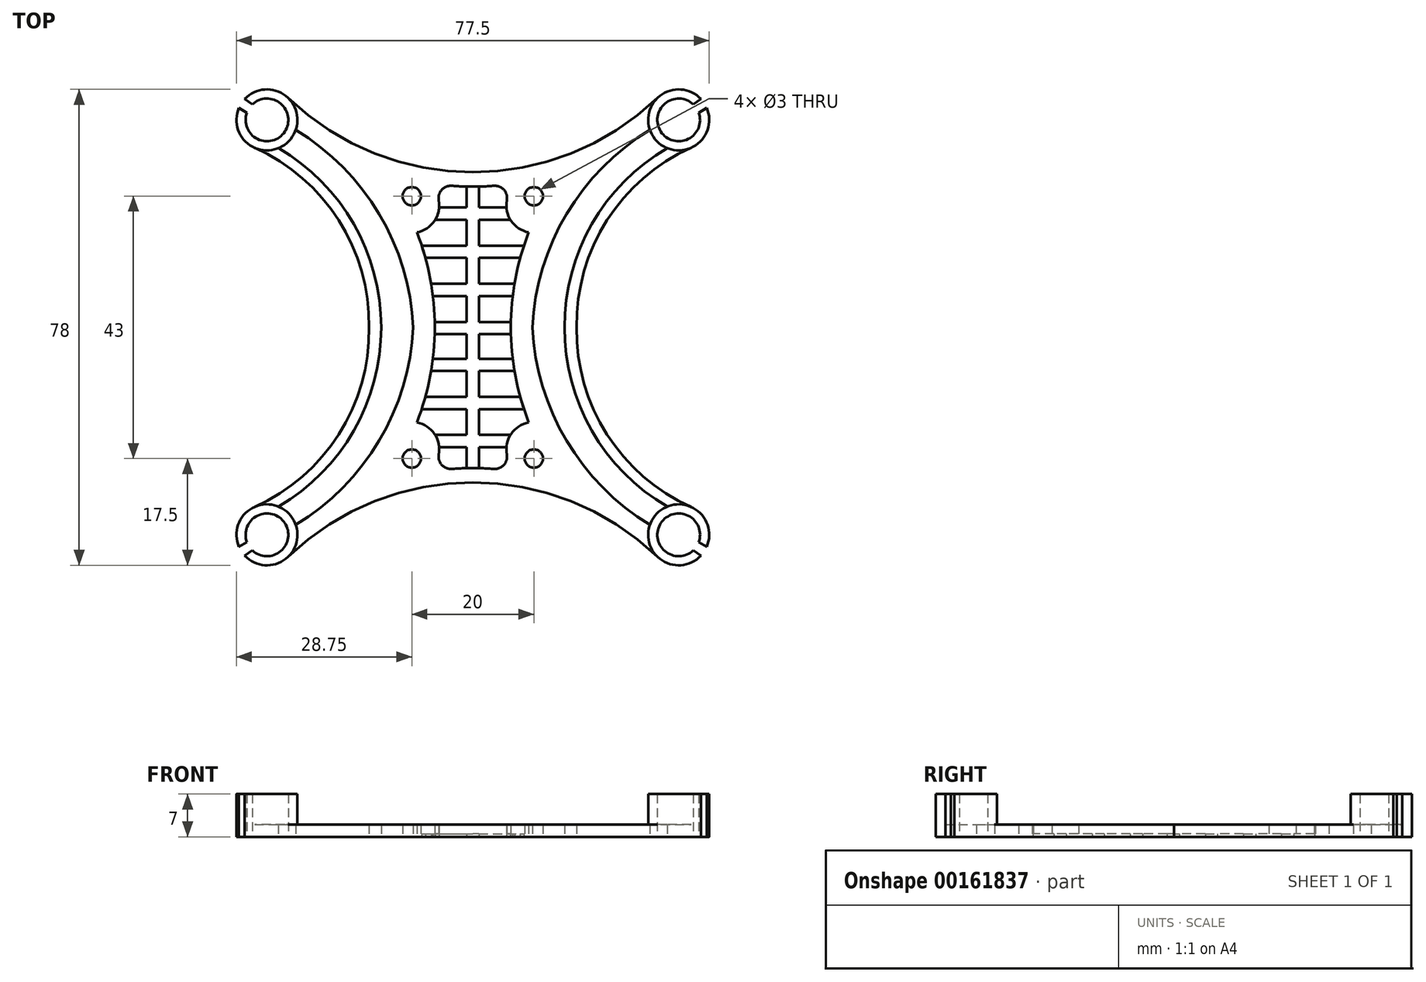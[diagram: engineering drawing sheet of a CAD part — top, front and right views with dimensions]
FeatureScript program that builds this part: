
annotation { "Feature Type Name" : "Feature", "Feature Type Description" : "" }
export const myFeature = defineFeature(function(context is Context, id is Id, definition is map)
    precondition{}
    {
        {
            var Q0;
            Q0=qCreatedBy(makeId("Top.planeOp"),FACE);
            var sketch = newSketch(context, id + "F0", { "sketchPlane" : qUnion([Q0])});
            skArc(sketch, "E0", {"start": v(37.04, -35.18) * mm, "mid": v(30.82, -32.08) * mm, "end": v(36.14, -36.56) * mm});
            skCircle(sketch, "E1", {"center": v(10, -21.5) * mm, "radius": 1.5 * mm});
            skArc(sketch, "E2", {"start": v(17.02, 0.03) * mm, "mid": v(21.97, -17.52) * mm, "end": v(35.78, -29.44) * mm});
            skLineSegment(sketch, "E3.MirrorCS", {"start": v(37.04, -35.18) * mm, "end": v(38.34, -35.99) * mm});
            skLineSegment(sketch, "E4.MirrorCS", {"start": v(36.14, -36.56) * mm, "end": v(37.39, -37.43) * mm});
            skArc(sketch, "E5.0", {"start": v(9.76, 0) * mm, "mid": v(15.37, -18.58) * mm, "end": v(29.04, -32.36) * mm});
            skArc(sketch, "E6.trimOffspring", {"start": v(9.16, -15.58) * mm, "mid": v(6.28, -17.47) * mm, "end": v(5.58, -20.84) * mm});
            skArc(sketch, "E7.trimOffspring", {"start": v(6.23, 0) * mm, "mid": v(6.97, -7.93) * mm, "end": v(9.16, -15.58) * mm});
            skArc(sketch, "E8.trimOffspring", {"start": v(0, -23.07) * mm, "mid": v(1.73, -23.1) * mm, "end": v(3.46, -23.2) * mm});
            skPoint(sketch, "E9.visualSharp", {"position": v(7.4, -23.67) * mm});
            skArc(sketch, "E9.filletArc", {"start": v(3.46, -23.2) * mm, "mid": v(5.1, -22.54) * mm, "end": v(5.58, -20.84) * mm});
            skArc(sketch, "E10.trimOffspring", {"start": v(15.01, 0) * mm, "mid": v(19.52, -16.95) * mm, "end": v(31.88, -29.4) * mm});
            skArc(sketch, "E11.trimOffspring", {"start": v(31.88, -29.4) * mm, "mid": v(30.14, -30.57) * mm, "end": v(29.04, -32.36) * mm});
            skArc(sketch, "E12.trimOffspring", {"start": v(38.34, -35.99) * mm, "mid": v(38.4, -32.19) * mm, "end": v(35.78, -29.44) * mm});
            skArc(sketch, "E13.MirrorCS", {"start": v(38.34, -35.99) * mm, "mid": v(38.74, -33.77) * mm, "end": v(38.13, -31.6) * mm});
            skArc(sketch, "E14.trimOffspring", {"start": v(30.28, -37.6) * mm, "mid": v(33.87, -39) * mm, "end": v(37.39, -37.43) * mm});
            skArc(sketch, "E15.MirrorCS", {"start": v(0, -23.07) * mm, "mid": v(-1.73, -23.1) * mm, "end": v(-3.46, -23.2) * mm});
            skLineSegment(sketch, "E16.MirrorCS", {"start": v(-36.14, -36.56) * mm, "end": v(-37.39, -37.43) * mm});
            skArc(sketch, "E17.MirrorCS", {"start": v(-34.5, -38.95) * mm, "mid": v(-36.07, -38.43) * mm, "end": v(-37.39, -37.43) * mm});
            skLineSegment(sketch, "E18.MirrorCS", {"start": v(-37.04, -35.18) * mm, "end": v(-38.34, -35.99) * mm});
            skArc(sketch, "E19.MirrorCS", {"start": v(-38.34, -35.99) * mm, "mid": v(-38.4, -32.19) * mm, "end": v(-35.78, -29.44) * mm});
            skArc(sketch, "E20.MirrorCS", {"start": v(-3.46, -23.2) * mm, "mid": v(-5.1, -22.54) * mm, "end": v(-5.58, -20.84) * mm});
            skArc(sketch, "E21.MirrorCS", {"start": v(-31.88, -29.4) * mm, "mid": v(-30.14, -30.57) * mm, "end": v(-29.04, -32.36) * mm});
            skArc(sketch, "E22.MirrorCS", {"start": v(-30.28, -37.6) * mm, "mid": v(-33.87, -39) * mm, "end": v(-37.39, -37.43) * mm});
            skArc(sketch, "E23.MirrorCS", {"start": v(-37.22, -30.41) * mm, "mid": v(-36.55, -29.86) * mm, "end": v(-35.78, -29.44) * mm});
            skCircle(sketch, "E24.MirrorC", {"center": v(-10, -21.5) * mm, "radius": 1.5 * mm});
            skArc(sketch, "E25.MirrorCS", {"start": v(-6.23, 0) * mm, "mid": v(-6.97, -7.93) * mm, "end": v(-9.16, -15.58) * mm});
            skArc(sketch, "E26.MirrorCS", {"start": v(-9.16, -15.58) * mm, "mid": v(-6.28, -17.47) * mm, "end": v(-5.58, -20.84) * mm});
            skPoint(sketch, "E27.MirrorP", {"position": v(-7.4, -23.67) * mm});
            skArc(sketch, "E28.MirrorCS", {"start": v(-9.76, 0) * mm, "mid": v(-15.37, -18.58) * mm, "end": v(-29.04, -32.36) * mm});
            skArc(sketch, "E29.MirrorCS", {"start": v(-37.04, -35.18) * mm, "mid": v(-30.82, -32.08) * mm, "end": v(-36.14, -36.56) * mm});
            skArc(sketch, "E30.MirrorCS", {"start": v(-17.02, 0.03) * mm, "mid": v(-21.97, -17.52) * mm, "end": v(-35.78, -29.44) * mm});
            skArc(sketch, "E31.MirrorCS", {"start": v(-15.01, 0) * mm, "mid": v(-19.52, -16.95) * mm, "end": v(-31.88, -29.4) * mm});
            skArc(sketch, "E32.MirrorCS", {"start": v(0, 23.07) * mm, "mid": v(1.73, 23.1) * mm, "end": v(3.46, 23.2) * mm});
            skArc(sketch, "E33.MirrorCS", {"start": v(0, 23.07) * mm, "mid": v(-1.73, 23.1) * mm, "end": v(-3.46, 23.2) * mm});
            skLineSegment(sketch, "E34.MirrorCS", {"start": v(-37.04, 35.18) * mm, "end": v(-38.34, 35.99) * mm});
            skLineSegment(sketch, "E35.MirrorCS", {"start": v(37.04, 35.18) * mm, "end": v(38.34, 35.99) * mm});
            skArc(sketch, "E36.MirrorCS", {"start": v(3.46, 23.2) * mm, "mid": v(5.1, 22.54) * mm, "end": v(5.58, 20.84) * mm});
            skLineSegment(sketch, "E37.MirrorCS", {"start": v(-36.14, 36.56) * mm, "end": v(-37.39, 37.43) * mm});
            skArc(sketch, "E38.MirrorCS", {"start": v(-30.28, 37.6) * mm, "mid": v(-33.87, 39) * mm, "end": v(-37.39, 37.43) * mm});
            skArc(sketch, "E39.MirrorCS", {"start": v(34.5, 38.95) * mm, "mid": v(36.07, 38.43) * mm, "end": v(37.39, 37.43) * mm});
            skLineSegment(sketch, "E40.MirrorCS", {"start": v(36.14, 36.56) * mm, "end": v(37.39, 37.43) * mm});
            skArc(sketch, "E41.MirrorCS", {"start": v(30.28, 37.6) * mm, "mid": v(33.87, 39) * mm, "end": v(37.39, 37.43) * mm});
            skArc(sketch, "E42.MirrorCS", {"start": v(-31.88, 29.4) * mm, "mid": v(-30.14, 30.57) * mm, "end": v(-29.04, 32.36) * mm});
            skArc(sketch, "E43.MirrorCS", {"start": v(31.88, 29.4) * mm, "mid": v(30.14, 30.57) * mm, "end": v(29.04, 32.36) * mm});
            skArc(sketch, "E44.MirrorCS", {"start": v(-34.5, 38.95) * mm, "mid": v(-36.07, 38.43) * mm, "end": v(-37.39, 37.43) * mm});
            skArc(sketch, "E45.MirrorCS", {"start": v(-3.46, 23.2) * mm, "mid": v(-5.1, 22.54) * mm, "end": v(-5.58, 20.84) * mm});
            skArc(sketch, "E46.MirrorCS", {"start": v(-37.04, 35.18) * mm, "mid": v(-30.82, 32.08) * mm, "end": v(-36.14, 36.56) * mm});
            skArc(sketch, "E47.MirrorCS", {"start": v(-38.34, 35.99) * mm, "mid": v(-38.4, 32.19) * mm, "end": v(-35.78, 29.44) * mm});
            skArc(sketch, "E48.MirrorCS", {"start": v(38.34, 35.99) * mm, "mid": v(38.74, 33.77) * mm, "end": v(38.13, 31.6) * mm});
            skArc(sketch, "E49.MirrorCS", {"start": v(37.04, 35.18) * mm, "mid": v(30.82, 32.08) * mm, "end": v(36.14, 36.56) * mm});
            skArc(sketch, "E50.MirrorCS", {"start": v(38.34, 35.99) * mm, "mid": v(38.4, 32.19) * mm, "end": v(35.78, 29.44) * mm});
            skCircle(sketch, "E51.MirrorC", {"center": v(10, 21.5) * mm, "radius": 1.5 * mm});
            skCircle(sketch, "E52.MirrorC", {"center": v(-10, 21.5) * mm, "radius": 1.5 * mm});
            skArc(sketch, "E53.MirrorCS", {"start": v(-38.34, 35.99) * mm, "mid": v(-38.74, 33.77) * mm, "end": v(-38.13, 31.6) * mm});
            skPoint(sketch, "E54.MirrorP", {"position": v(-7.4, 23.67) * mm});
            skPoint(sketch, "E55.MirrorP", {"position": v(7.4, 23.67) * mm});
            skArc(sketch, "E56.MirrorCS", {"start": v(-15.01, 0) * mm, "mid": v(-19.52, 16.95) * mm, "end": v(-31.88, 29.4) * mm});
            skArc(sketch, "E57.MirrorCS", {"start": v(6.23, 0) * mm, "mid": v(6.97, 7.93) * mm, "end": v(9.16, 15.58) * mm});
            skArc(sketch, "E58.MirrorCS", {"start": v(-6.23, 0) * mm, "mid": v(-6.97, 7.93) * mm, "end": v(-9.16, 15.58) * mm});
            skArc(sketch, "E59.MirrorCS", {"start": v(-17.02, -0.03) * mm, "mid": v(-21.97, 17.52) * mm, "end": v(-35.78, 29.44) * mm});
            skArc(sketch, "E60.MirrorCS", {"start": v(-9.76, 0) * mm, "mid": v(-15.37, 18.58) * mm, "end": v(-29.04, 32.36) * mm});
            skArc(sketch, "E61.MirrorCS", {"start": v(15.01, 0) * mm, "mid": v(19.52, 16.95) * mm, "end": v(31.88, 29.4) * mm});
            skArc(sketch, "E62.MirrorCS", {"start": v(9.76, 0) * mm, "mid": v(15.37, 18.58) * mm, "end": v(29.04, 32.36) * mm});
            skArc(sketch, "E63.MirrorCS", {"start": v(9.16, 15.58) * mm, "mid": v(6.28, 17.47) * mm, "end": v(5.58, 20.84) * mm});
            skArc(sketch, "E64.MirrorCS", {"start": v(-9.16, 15.58) * mm, "mid": v(-6.28, 17.47) * mm, "end": v(-5.58, 20.84) * mm});
            skArc(sketch, "E65.MirrorCS", {"start": v(17.02, -0.03) * mm, "mid": v(21.97, 17.52) * mm, "end": v(35.78, 29.44) * mm});
            skArc(sketch, "E66", {"start": v(-30.28, 37.6) * mm, "mid": v(0, 25.42) * mm, "end": v(30.28, 37.6) * mm});
            skPoint(sketch, "E67.MirrorCS.start.orphan", {"position": v(0, 25.42) * mm});
            skArc(sketch, "E68.MirrorCS", {"start": v(-30.28, -37.6) * mm, "mid": v(0, -25.42) * mm, "end": v(30.28, -37.6) * mm});
            skSolve(sketch);
        }
        {
            var Q0;
            Q0=qSketchRegion(id+"F0",true);
            extrude(context, id + "F1", {"entities" : qUnion([Q0]), "depth" : 2 * mm});
        }
        {
            var Q0;
            Q0=makeQuery(id+"F1.opExtrude","CAP_FACE",FACE,{"disambiguationData":[OSD([sQuery(id+"F0.wireOp",EDGE,"07ed9256-dc37-4db6-ad36-5c41a7523dda2.MirrorCS"),sQuery(id+"F0.wireOp",EDGE,"07ed9256-dc37-4db6-ad36-5c41a7523dda3.MirrorCS"),sQuery(id+"F0.wireOp",EDGE,"07ed9256-dc37-4db6-ad36-5c41a7523dda4.MirrorCS"),sQuery(id+"F0.wireOp",EDGE,"07ed9256-dc37-4db6-ad36-5c41a7523dda5.MirrorCS"),sQuery(id+"F0.wireOp",EDGE,"E9.filletArc"),sQuery(id+"F0.wireOp",EDGE,"E8.trimOffspring"),sQuery(id+"F0.wireOp",EDGE,"07ed9256-dc37-4db6-ad36-5c41a7523dda8.MirrorCS"),sQuery(id+"F0.wireOp",EDGE,"E11.trimOffspring"),sQuery(id+"F0.wireOp",EDGE,"E13.MirrorCS"),sQuery(id+"F0.wireOp",EDGE,"07ed9256-dc37-4db6-ad36-5c41a7523dda11.MirrorCS"),sQuery(id+"F0.wireOp",EDGE,"E4.MirrorCS"),sQuery(id+"F0.wireOp",EDGE,"E3.MirrorCS"),sQuery(id+"F0.wireOp",EDGE,"07ed9256-dc37-4db6-ad36-5c41a7523dda14.MirrorCS"),sQuery(id+"F0.wireOp",EDGE,"E1"),sQuery(id+"F0.wireOp",EDGE,"07ed9256-dc37-4db6-ad36-5c41a7523dda16.MirrorC"),sQuery(id+"F0.wireOp",EDGE,"07ed9256-dc37-4db6-ad36-5c41a7523dda17.MirrorCS"),sQuery(id+"F0.wireOp",EDGE,"07ed9256-dc37-4db6-ad36-5c41a7523dda18.MirrorCS"),sQuery(id+"F0.wireOp",EDGE,"07ed9256-dc37-4db6-ad36-5c41a7523dda19.MirrorCS"),sQuery(id+"F0.wireOp",EDGE,"E10.trimOffspring"),sQuery(id+"F0.wireOp",EDGE,"07ed9256-dc37-4db6-ad36-5c41a7523dda21.MirrorCS"),sQuery(id+"F0.wireOp",EDGE,"07ed9256-dc37-4db6-ad36-5c41a7523dda22.MirrorCS"),sQuery(id+"F0.wireOp",EDGE,"07ed9256-dc37-4db6-ad36-5c41a7523dda23.MirrorCS"),sQuery(id+"F0.wireOp",EDGE,"E5.0"),sQuery(id+"F0.wireOp",EDGE,"E0"),sQuery(id+"F0.wireOp",EDGE,"E6.trimOffspring"),sQuery(id+"F0.wireOp",EDGE,"E2"),sQuery(id+"F0.wireOp",EDGE,"07ed9256-dc37-4db6-ad36-5c41a7523dda29.MirrorCS"),sQuery(id+"F0.wireOp",EDGE,"E7.trimOffspring"),sQuery(id+"F0.wireOp",EDGE,"07ed9256-dc37-4db6-ad36-5c41a7523dda31.MirrorCS"),sQuery(id+"F0.wireOp",EDGE,"07ed9256-dc37-4db6-ad36-5c41a7523dda33.MirrorCS"),sQuery(id+"F0.wireOp",EDGE,"966d41c8-d036-42bd-8d6f-7643b6f02c428.MirrorCS"),sQuery(id+"F0.wireOp",EDGE,"966d41c8-d036-42bd-8d6f-7643b6f02c429.MirrorCS"),sQuery(id+"F0.wireOp",EDGE,"966d41c8-d036-42bd-8d6f-7643b6f02c4210.MirrorCS"),sQuery(id+"F0.wireOp",EDGE,"966d41c8-d036-42bd-8d6f-7643b6f02c4211.MirrorCS"),sQuery(id+"F0.wireOp",EDGE,"966d41c8-d036-42bd-8d6f-7643b6f02c4217.MirrorCS"),sQuery(id+"F0.wireOp",EDGE,"966d41c8-d036-42bd-8d6f-7643b6f02c4222.MirrorCS"),sQuery(id+"F0.wireOp",EDGE,"966d41c8-d036-42bd-8d6f-7643b6f02c4225.MirrorCS"),sQuery(id+"F0.wireOp",EDGE,"966d41c8-d036-42bd-8d6f-7643b6f02c4226.MirrorCS"),sQuery(id+"F0.wireOp",EDGE,"966d41c8-d036-42bd-8d6f-7643b6f02c4227.MirrorCS"),sQuery(id+"F0.wireOp",EDGE,"966d41c8-d036-42bd-8d6f-7643b6f02c4228.MirrorCS"),sQuery(id+"F0.wireOp",EDGE,"966d41c8-d036-42bd-8d6f-7643b6f02c4229.MirrorCS"),sQuery(id+"F0.wireOp",EDGE,"966d41c8-d036-42bd-8d6f-7643b6f02c4230.MirrorCS"),sQuery(id+"F0.wireOp",EDGE,"966d41c8-d036-42bd-8d6f-7643b6f02c4231.MirrorCS"),sQuery(id+"F0.wireOp",EDGE,"966d41c8-d036-42bd-8d6f-7643b6f02c4232.MirrorCS"),sQuery(id+"F0.wireOp",EDGE,"966d41c8-d036-42bd-8d6f-7643b6f02c4233.MirrorCS"),sQuery(id+"F0.wireOp",EDGE,"966d41c8-d036-42bd-8d6f-7643b6f02c4236.MirrorC"),sQuery(id+"F0.wireOp",EDGE,"966d41c8-d036-42bd-8d6f-7643b6f02c4237.MirrorC"),sQuery(id+"F0.wireOp",EDGE,"966d41c8-d036-42bd-8d6f-7643b6f02c4253.MirrorCS"),sQuery(id+"F0.wireOp",EDGE,"966d41c8-d036-42bd-8d6f-7643b6f02c4254.MirrorCS"),sQuery(id+"F0.wireOp",EDGE,"966d41c8-d036-42bd-8d6f-7643b6f02c4255.MirrorCS"),sQuery(id+"F0.wireOp",EDGE,"966d41c8-d036-42bd-8d6f-7643b6f02c4256.MirrorCS"),sQuery(id+"F0.wireOp",EDGE,"966d41c8-d036-42bd-8d6f-7643b6f02c4257.MirrorCS"),sQuery(id+"F0.wireOp",EDGE,"966d41c8-d036-42bd-8d6f-7643b6f02c4259.MirrorCS"),sQuery(id+"F0.wireOp",EDGE,"966d41c8-d036-42bd-8d6f-7643b6f02c4260.MirrorCS"),sQuery(id+"F0.wireOp",EDGE,"966d41c8-d036-42bd-8d6f-7643b6f02c4262.MirrorCS"),sQuery(id+"F0.wireOp",EDGE,"966d41c8-d036-42bd-8d6f-7643b6f02c4263.MirrorCS"),sQuery(id+"F0.wireOp",EDGE,"966d41c8-d036-42bd-8d6f-7643b6f02c4264.MirrorCS"),sQuery(id+"F0.wireOp",EDGE,"966d41c8-d036-42bd-8d6f-7643b6f02c4265.MirrorCS"),sQuery(id+"F0.wireOp",EDGE,"966d41c8-d036-42bd-8d6f-7643b6f02c4266.MirrorCS"),sQuery(id+"F0.wireOp",EDGE,"966d41c8-d036-42bd-8d6f-7643b6f02c4267.MirrorCS")])],"isStart":false});
            var sketch = newSketch(context, id + "F2", { "sketchPlane" : qUnion([Q0])});
            skArc(sketch, "E69.0", {"start": v(37.04, -35.18) * mm, "mid": v(30.82, -32.08) * mm, "end": v(36.14, -36.56) * mm});
            skLineSegment(sketch, "E70.0", {"start": v(37.04, -35.18) * mm, "end": v(38.34, -35.99) * mm});
            skLineSegment(sketch, "E70.1", {"start": v(36.14, -36.56) * mm, "end": v(36.14, -36.56) * mm});
            skLineSegment(sketch, "E71.MirrorCS", {"start": v(-37.04, -35.18) * mm, "end": v(-38.34, -35.99) * mm});
            skLineSegment(sketch, "E72.MirrorCS", {"start": v(-36.14, -36.56) * mm, "end": v(-36.14, -36.56) * mm});
            skArc(sketch, "E73.MirrorCS", {"start": v(-37.04, -35.18) * mm, "mid": v(-30.82, -32.08) * mm, "end": v(-36.14, -36.56) * mm});
            skLineSegment(sketch, "E74.MirrorCS", {"start": v(37.04, 35.18) * mm, "end": v(38.34, 35.99) * mm});
            skLineSegment(sketch, "E75.MirrorCS", {"start": v(36.14, 36.56) * mm, "end": v(36.14, 36.56) * mm});
            skLineSegment(sketch, "E76.MirrorCS", {"start": v(-37.04, 35.18) * mm, "end": v(-38.34, 35.99) * mm});
            skLineSegment(sketch, "E77.MirrorCS", {"start": v(-36.14, 36.56) * mm, "end": v(-36.14, 36.56) * mm});
            skArc(sketch, "E78.MirrorCS", {"start": v(-37.04, 35.18) * mm, "mid": v(-30.82, 32.08) * mm, "end": v(-36.14, 36.56) * mm});
            skArc(sketch, "E79.MirrorCS", {"start": v(37.04, 35.18) * mm, "mid": v(30.82, 32.08) * mm, "end": v(36.14, 36.56) * mm});
            skArc(sketch, "E80", {"start": v(38.34, -35.99) * mm, "mid": v(29.57, -31.26) * mm, "end": v(37.39, -37.43) * mm});
            skArc(sketch, "E81", {"start": v(-38.34, 35.99) * mm, "mid": v(-29.57, 31.26) * mm, "end": v(-37.39, 37.43) * mm});
            skArc(sketch, "E82", {"start": v(37.39, 37.43) * mm, "mid": v(29.57, 31.26) * mm, "end": v(38.34, 35.99) * mm});
            skArc(sketch, "E83", {"start": v(-37.39, -37.43) * mm, "mid": v(-29.57, -31.26) * mm, "end": v(-38.34, -35.99) * mm});
            skLineSegment(sketch, "E84", {"start": v(36.14, -36.56) * mm, "end": v(37.39, -37.43) * mm});
            skLineSegment(sketch, "E85", {"start": v(-37.39, -37.43) * mm, "end": v(-36.14, -36.56) * mm});
            skLineSegment(sketch, "E86", {"start": v(36.14, 36.56) * mm, "end": v(37.39, 37.43) * mm});
            skLineSegment(sketch, "E87", {"start": v(-36.14, 36.56) * mm, "end": v(-37.39, 37.43) * mm});
            skSolve(sketch);
        }
        {
            var Q0;
            Q0=qSketchRegion(id+"F2",true);
            extrude(context, id + "F3", {"entities" : qUnion([Q0]), "operationType" : NewBodyOperationType.ADD, "depth" : 5 * mm});
        }
        {
            var Q0;
            Q0=qCreatedBy(makeId("Top.planeOp"),FACE);
            var sketch = newSketch(context, id + "F4", { "sketchPlane" : qUnion([Q0])});
            skArc(sketch, "E88.0", {"start": v(-6.23, 0) * mm, "mid": v(-6.97, 7.93) * mm, "end": v(-9.16, 15.58) * mm});
            skArc(sketch, "E88.1", {"start": v(-9.16, 15.58) * mm, "mid": v(-6.28, 17.47) * mm, "end": v(-5.58, 20.84) * mm});
            skArc(sketch, "E88.2", {"start": v(-3.46, 23.2) * mm, "mid": v(-5.1, 22.54) * mm, "end": v(-5.58, 20.84) * mm});
            skArc(sketch, "E88.3", {"start": v(0, 23.07) * mm, "mid": v(-1.73, 23.1) * mm, "end": v(-3.46, 23.2) * mm});
            skArc(sketch, "E88.4", {"start": v(0, 23.07) * mm, "mid": v(1.73, 23.1) * mm, "end": v(3.46, 23.2) * mm});
            skArc(sketch, "E88.5", {"start": v(3.46, 23.2) * mm, "mid": v(5.1, 22.54) * mm, "end": v(5.58, 20.84) * mm});
            skArc(sketch, "E88.6", {"start": v(9.16, 15.58) * mm, "mid": v(6.28, 17.47) * mm, "end": v(5.58, 20.84) * mm});
            skArc(sketch, "E88.7", {"start": v(6.23, 0) * mm, "mid": v(6.97, 7.93) * mm, "end": v(9.16, 15.58) * mm});
            skArc(sketch, "E88.8", {"start": v(9.16, -15.58) * mm, "mid": v(6.28, -17.47) * mm, "end": v(5.58, -20.84) * mm});
            skArc(sketch, "E88.9", {"start": v(6.23, 0) * mm, "mid": v(6.97, -7.93) * mm, "end": v(9.16, -15.58) * mm});
            skArc(sketch, "E88.10", {"start": v(3.46, -23.2) * mm, "mid": v(5.1, -22.54) * mm, "end": v(5.58, -20.84) * mm});
            skArc(sketch, "E88.11", {"start": v(0, -23.07) * mm, "mid": v(1.73, -23.1) * mm, "end": v(3.46, -23.2) * mm});
            skArc(sketch, "E88.12", {"start": v(0, -23.07) * mm, "mid": v(-1.73, -23.1) * mm, "end": v(-3.46, -23.2) * mm});
            skArc(sketch, "E88.13", {"start": v(-3.46, -23.2) * mm, "mid": v(-5.1, -22.54) * mm, "end": v(-5.58, -20.84) * mm});
            skArc(sketch, "E88.14", {"start": v(-9.16, -15.58) * mm, "mid": v(-6.28, -17.47) * mm, "end": v(-5.58, -20.84) * mm});
            skArc(sketch, "E88.15", {"start": v(-6.23, 0) * mm, "mid": v(-6.97, -7.93) * mm, "end": v(-9.16, -15.58) * mm});
            skLineSegment(sketch, "E89.0", {"start": v(-6.24, 0.9) * mm, "end": v(-1, 0.9) * mm});
            skLineSegment(sketch, "E90.0", {"start": v(-6.25, -1.1) * mm, "end": v(-1, -1.1) * mm});
            skLineSegment(sketch, "E91.0.1.0", {"start": v(-6.54, 5.14) * mm, "end": v(-1, 5.14) * mm});
            skLineSegment(sketch, "E91.0.1.1", {"start": v(-6.83, 7.14) * mm, "end": v(-1, 7.14) * mm});
            skLineSegment(sketch, "E91.0.2.0", {"start": v(-7.77, 11.4) * mm, "end": v(-1, 11.4) * mm});
            skLineSegment(sketch, "E91.0.2.1", {"start": v(-8.37, 13.4) * mm, "end": v(-1, 13.4) * mm});
            skLineSegment(sketch, "E91.0.3.0", {"start": v(-6.17, 17.64) * mm, "end": v(-1, 17.64) * mm});
            skLineSegment(sketch, "E91.0.3.1", {"start": v(-5.51, 19.64) * mm, "end": v(-1, 19.64) * mm});
            skLineSegment(sketch, "E92.MirrorCS", {"start": v(-6.17, -17.64) * mm, "end": v(-1, -17.64) * mm});
            skLineSegment(sketch, "E93.MirrorCS", {"start": v(-8.37, -13.4) * mm, "end": v(-1, -13.4) * mm});
            skLineSegment(sketch, "E94.MirrorCS", {"start": v(-7.77, -11.4) * mm, "end": v(-1, -11.4) * mm});
            skLineSegment(sketch, "E95.MirrorCS", {"start": v(-6.83, -7.14) * mm, "end": v(-1, -7.14) * mm});
            skLineSegment(sketch, "E96.MirrorCS", {"start": v(-6.54, -5.14) * mm, "end": v(-1, -5.14) * mm});
            skLineSegment(sketch, "E97.MirrorCS", {"start": v(-5.51, -19.64) * mm, "end": v(-1, -19.64) * mm});
            skPoint(sketch, "E98.orphan", {"position": v(-6.23, 13.4) * mm});
            skPoint(sketch, "E99.orphan", {"position": v(-6.23, 11.4) * mm});
            skPoint(sketch, "E100.orphan", {"position": v(6.23, 11.4) * mm});
            skPoint(sketch, "E101.orphan", {"position": v(6.23, 13.4) * mm});
            skPoint(sketch, "E102.orphan", {"position": v(6.23, 7.14) * mm});
            skPoint(sketch, "E103.orphan", {"position": v(6.23, 5.14) * mm});
            skPoint(sketch, "E104.orphan", {"position": v(-6.23, 7.14) * mm});
            skPoint(sketch, "E105.orphan", {"position": v(-6.23, -5.14) * mm});
            skPoint(sketch, "E106.orphan", {"position": v(-6.23, -7.14) * mm});
            skPoint(sketch, "E107.orphan", {"position": v(6.23, -7.14) * mm});
            skPoint(sketch, "E108.orphan", {"position": v(6.23, -5.14) * mm});
            skPoint(sketch, "E109.orphan", {"position": v(6.23, -11.4) * mm});
            skPoint(sketch, "E110.orphan", {"position": v(6.23, -13.4) * mm});
            skPoint(sketch, "E111.orphan", {"position": v(-6.23, -13.4) * mm});
            skPoint(sketch, "E112.orphan", {"position": v(-6.23, -11.4) * mm});
            skPoint(sketch, "E113.orphan", {"position": v(-6.23, -19.64) * mm});
            skPoint(sketch, "E114.orphan", {"position": v(-6.23, -17.64) * mm});
            skPoint(sketch, "E115.orphan", {"position": v(6.23, -19.64) * mm});
            skPoint(sketch, "E116.orphan", {"position": v(6.23, -17.64) * mm});
            skLineSegment(sketch, "E117.0", {"start": v(-1, 23.08) * mm, "end": v(-1, 19.64) * mm});
            skLineSegment(sketch, "E118.0", {"start": v(1, 23.08) * mm, "end": v(1, 19.64) * mm});
            skLineSegment(sketch, "E119.trimOffspring", {"start": v(1, -19.64) * mm, "end": v(1, -23.08) * mm});
            skLineSegment(sketch, "E120.trimOffspring", {"start": v(1, -19.64) * mm, "end": v(5.51, -19.64) * mm});
            skLineSegment(sketch, "E121.trimOffspring", {"start": v(1, -17.64) * mm, "end": v(6.17, -17.64) * mm});
            skLineSegment(sketch, "E122.trimOffspring", {"start": v(-1, -19.64) * mm, "end": v(-1, -23.08) * mm});
            skLineSegment(sketch, "E123.trimOffspring", {"start": v(1, -11.4) * mm, "end": v(7.77, -11.4) * mm});
            skLineSegment(sketch, "E124.trimOffspring", {"start": v(1, -13.4) * mm, "end": v(1, -17.64) * mm});
            skLineSegment(sketch, "E125.trimOffspring", {"start": v(1, -13.4) * mm, "end": v(8.37, -13.4) * mm});
            skLineSegment(sketch, "E126.trimOffspring", {"start": v(-1, -13.4) * mm, "end": v(-1, -17.64) * mm});
            skLineSegment(sketch, "E127.trimOffspring", {"start": v(1, -7.14) * mm, "end": v(6.83, -7.14) * mm});
            skLineSegment(sketch, "E128.trimOffspring", {"start": v(1, -5.14) * mm, "end": v(6.54, -5.14) * mm});
            skLineSegment(sketch, "E129.trimOffspring", {"start": v(1, -1.1) * mm, "end": v(6.25, -1.1) * mm});
            skLineSegment(sketch, "E130.trimOffspring", {"start": v(1, -1.1) * mm, "end": v(1, -5.14) * mm});
            skLineSegment(sketch, "E131.trimOffspring", {"start": v(-1, -1.1) * mm, "end": v(-1, -5.14) * mm});
            skLineSegment(sketch, "E132.trimOffspring", {"start": v(-1, -7.14) * mm, "end": v(-1, -11.4) * mm});
            skLineSegment(sketch, "E133.trimOffspring", {"start": v(1, -7.14) * mm, "end": v(1, -11.4) * mm});
            skLineSegment(sketch, "E134.trimOffspring", {"start": v(1, 5.14) * mm, "end": v(1, 0.9) * mm});
            skLineSegment(sketch, "E135.trimOffspring", {"start": v(-1, 5.14) * mm, "end": v(-1, 0.9) * mm});
            skLineSegment(sketch, "E136.trimOffspring", {"start": v(1, 5.14) * mm, "end": v(6.54, 5.14) * mm});
            skLineSegment(sketch, "E137.trimOffspring", {"start": v(1, 0.9) * mm, "end": v(6.24, 0.9) * mm});
            skLineSegment(sketch, "E138.trimOffspring", {"start": v(1, 7.14) * mm, "end": v(6.83, 7.14) * mm});
            skLineSegment(sketch, "E139.trimOffspring", {"start": v(1, 13.4) * mm, "end": v(8.37, 13.4) * mm});
            skLineSegment(sketch, "E140.trimOffspring", {"start": v(1, 11.4) * mm, "end": v(7.77, 11.4) * mm});
            skLineSegment(sketch, "E141.trimOffspring", {"start": v(-1, 11.4) * mm, "end": v(-1, 7.14) * mm});
            skLineSegment(sketch, "E142.trimOffspring", {"start": v(1, 11.4) * mm, "end": v(1, 7.14) * mm});
            skLineSegment(sketch, "E143.trimOffspring", {"start": v(-1, 17.64) * mm, "end": v(-1, 13.4) * mm});
            skLineSegment(sketch, "E144.trimOffspring", {"start": v(1, 17.64) * mm, "end": v(1, 13.4) * mm});
            skLineSegment(sketch, "E145.trimOffspring", {"start": v(1, 17.64) * mm, "end": v(6.17, 17.64) * mm});
            skLineSegment(sketch, "E146.trimOffspring", {"start": v(1, 19.64) * mm, "end": v(5.51, 19.64) * mm});
            skSolve(sketch);
        }
        {
            var Q0;
            {var subQ45=sQuery(id+"F4.wireOp",EDGE,"E89.0");Q0=makeQuery(id+"F4.imprint","IMPRINT",FACE,{"disambiguationData":[TD([[makeQuery(id+"F4.imprint","IMPRINT",EDGE,{"derivedFrom":subQ45}),-1.0]])]});}
            extrude(context, id + "F5", {"entities" : qUnion([Q0]), "operationType" : NewBodyOperationType.ADD, "depth" : .5 * mm});
        }
    });
